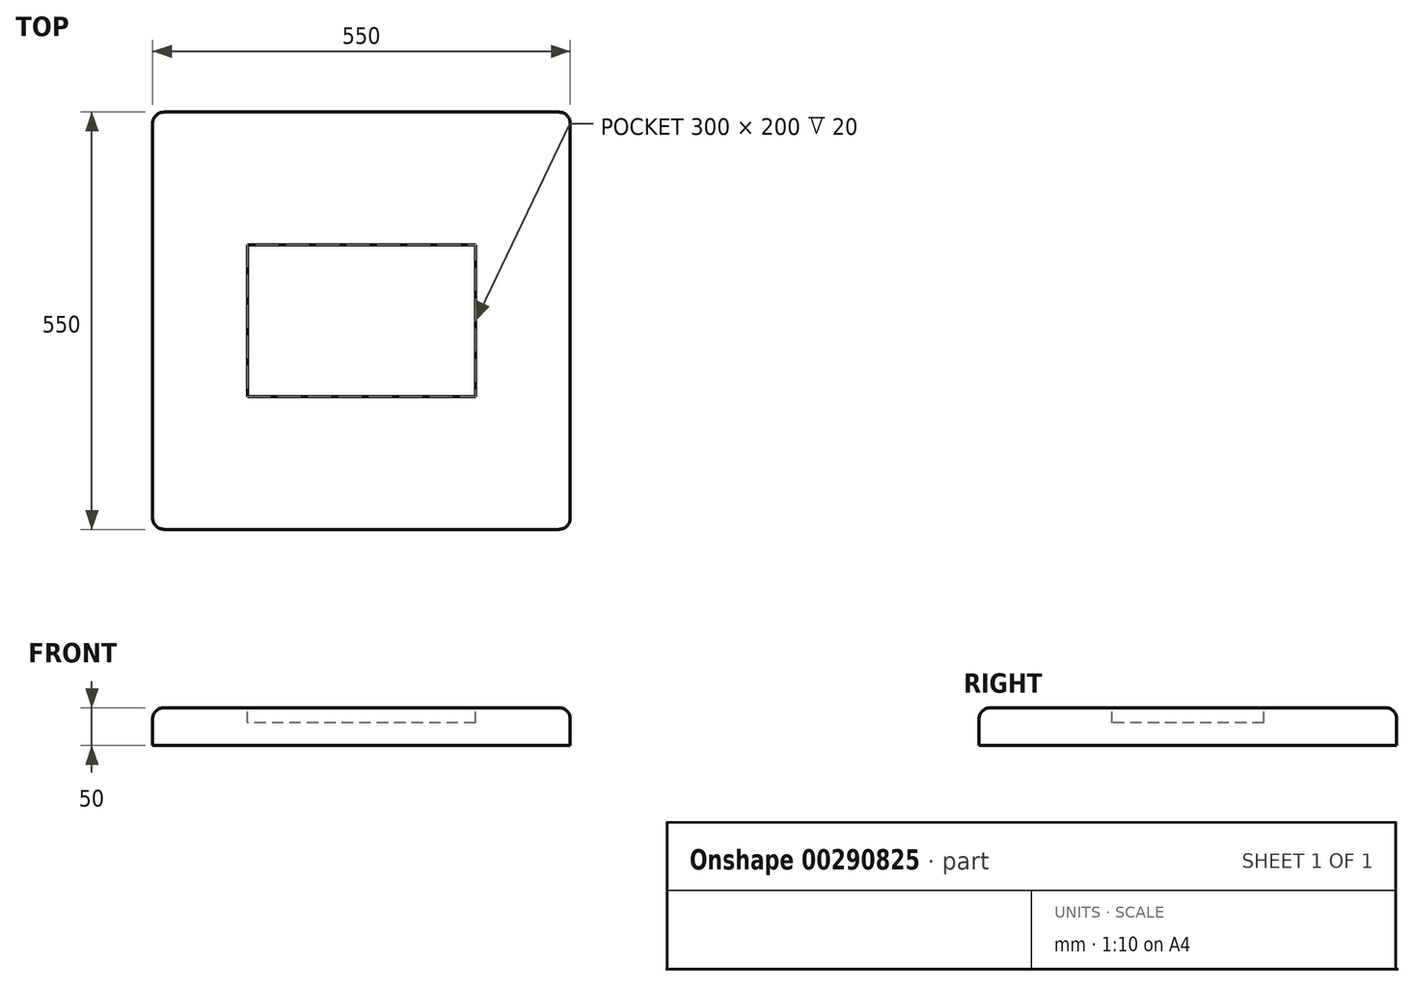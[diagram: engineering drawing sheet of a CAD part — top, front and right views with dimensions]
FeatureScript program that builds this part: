
annotation { "Feature Type Name" : "Feature", "Feature Type Description" : "" }
export const myFeature = defineFeature(function(context is Context, id is Id, definition is map)
    precondition{}
    {
        {
            var Q0;
            Q0=qCreatedBy(makeId("Top.planeOp"),FACE);
            var sketch = newSketch(context, id + "F0", { "sketchPlane" : qUnion([Q0])});
            skLineSegment(sketch, "E0.bottom", {"start": v(275, 275) * mm, "end": v(-275, 275) * mm});
            skLineSegment(sketch, "E0.top", {"start": v(275, -275) * mm, "end": v(-275, -275) * mm});
            skLineSegment(sketch, "E0.left", {"start": v(275, 275) * mm, "end": v(275, -275) * mm});
            skLineSegment(sketch, "E0.right", {"start": v(-275, 275) * mm, "end": v(-275, -275) * mm});
            skPoint(sketch, "E0.middle", {"position": v(0, 0) * mm});
            skSolve(sketch);
        }
        {
            var Q0;
            Q0 = qSketchRegion(id + "F0", true);
            extrude(context, id + "F1", {"entities" : qUnion([Q0]), "depth" : 50 * mm});
        }
        {
            var Q0;
            Q0=makeQuery(id+"F1.opExtrude","CAP_EDGE",EDGE,{"disambiguationData":[OSD([sQuery(id+"F0.wireOp",EDGE,"E0.top")])],"isStart":false});
            var Q1;
            Q1=makeQuery(id+"F1.opExtrude","CAP_EDGE",EDGE,{"disambiguationData":[OSD([sQuery(id+"F0.wireOp",EDGE,"E0.left")])],"isStart":false});
            var Q2;
            Q2=makeQuery(id+"F1.opExtrude","CAP_EDGE",EDGE,{"disambiguationData":[OSD([sQuery(id+"F0.wireOp",EDGE,"E0.bottom")])],"isStart":false});
            var Q3;
            Q3=makeQuery(id+"F1.opExtrude","CAP_EDGE",EDGE,{"disambiguationData":[OSD([sQuery(id+"F0.wireOp",EDGE,"E0.right")])],"isStart":false});
            var Q4;
            Q4=makeQuery(id+"F1.opExtrude","SWEPT_EDGE",EDGE,{"disambiguationData":[OSD([sQuery(id+"F0.wireOp",EDGE,"E0.top"),sQuery(id+"F0.wireOp",EDGE,"E0.left")])]});
            var Q5;
            Q5=makeQuery(id+"F1.opExtrude","SWEPT_EDGE",EDGE,{"disambiguationData":[OSD([sQuery(id+"F0.wireOp",EDGE,"E0.bottom"),sQuery(id+"F0.wireOp",EDGE,"E0.left")])]});
            var Q6;
            Q6=makeQuery(id+"F1.opExtrude","SWEPT_EDGE",EDGE,{"disambiguationData":[OSD([sQuery(id+"F0.wireOp",EDGE,"E0.bottom"),sQuery(id+"F0.wireOp",EDGE,"E0.right")])]});
            var Q7;
            Q7=makeQuery(id+"F1.opExtrude","SWEPT_EDGE",EDGE,{"disambiguationData":[OSD([sQuery(id+"F0.wireOp",EDGE,"E0.top"),sQuery(id+"F0.wireOp",EDGE,"E0.right")])]});
            fillet(context, id + "F2", {"entities" : qUnion([Q0, Q1, Q2, Q3, Q4, Q5, Q6, Q7]), "radius" : 15 * mm, "tangentPropagation" : true, "allowEdgeOverflow" : false});
        }
        {
            var Q0;
            Q0=makeQuery(id+"F1.opExtrude","CAP_FACE",FACE,{"disambiguationData":[OSD([sQuery(id+"F0.wireOp",EDGE,"E0.bottom"),sQuery(id+"F0.wireOp",EDGE,"E0.top"),sQuery(id+"F0.wireOp",EDGE,"E0.left"),sQuery(id+"F0.wireOp",EDGE,"E0.right")])],"isStart":false});
            var sketch = newSketch(context, id + "F3", { "sketchPlane" : qUnion([Q0])});
            skLineSegment(sketch, "E1.bottom", {"start": v(150, 100) * mm, "end": v(-150, 100) * mm});
            skLineSegment(sketch, "E1.top", {"start": v(150, -100) * mm, "end": v(-150, -100) * mm});
            skLineSegment(sketch, "E1.left", {"start": v(150, 100) * mm, "end": v(150, -100) * mm});
            skLineSegment(sketch, "E1.right", {"start": v(-150, 100) * mm, "end": v(-150, -100) * mm});
            skPoint(sketch, "E1.middle", {"position": v(0, 0) * mm});
            skSolve(sketch);
        }
        {
            var Q0;
            Q0 = qSketchRegion(id + "F3", true);
            extrude(context, id + "F4", {"entities" : qUnion([Q0]), "operationType" : NewBodyOperationType.REMOVE, "oppositeDirection" : true, "depth" : 20 * mm});
        }
    });
